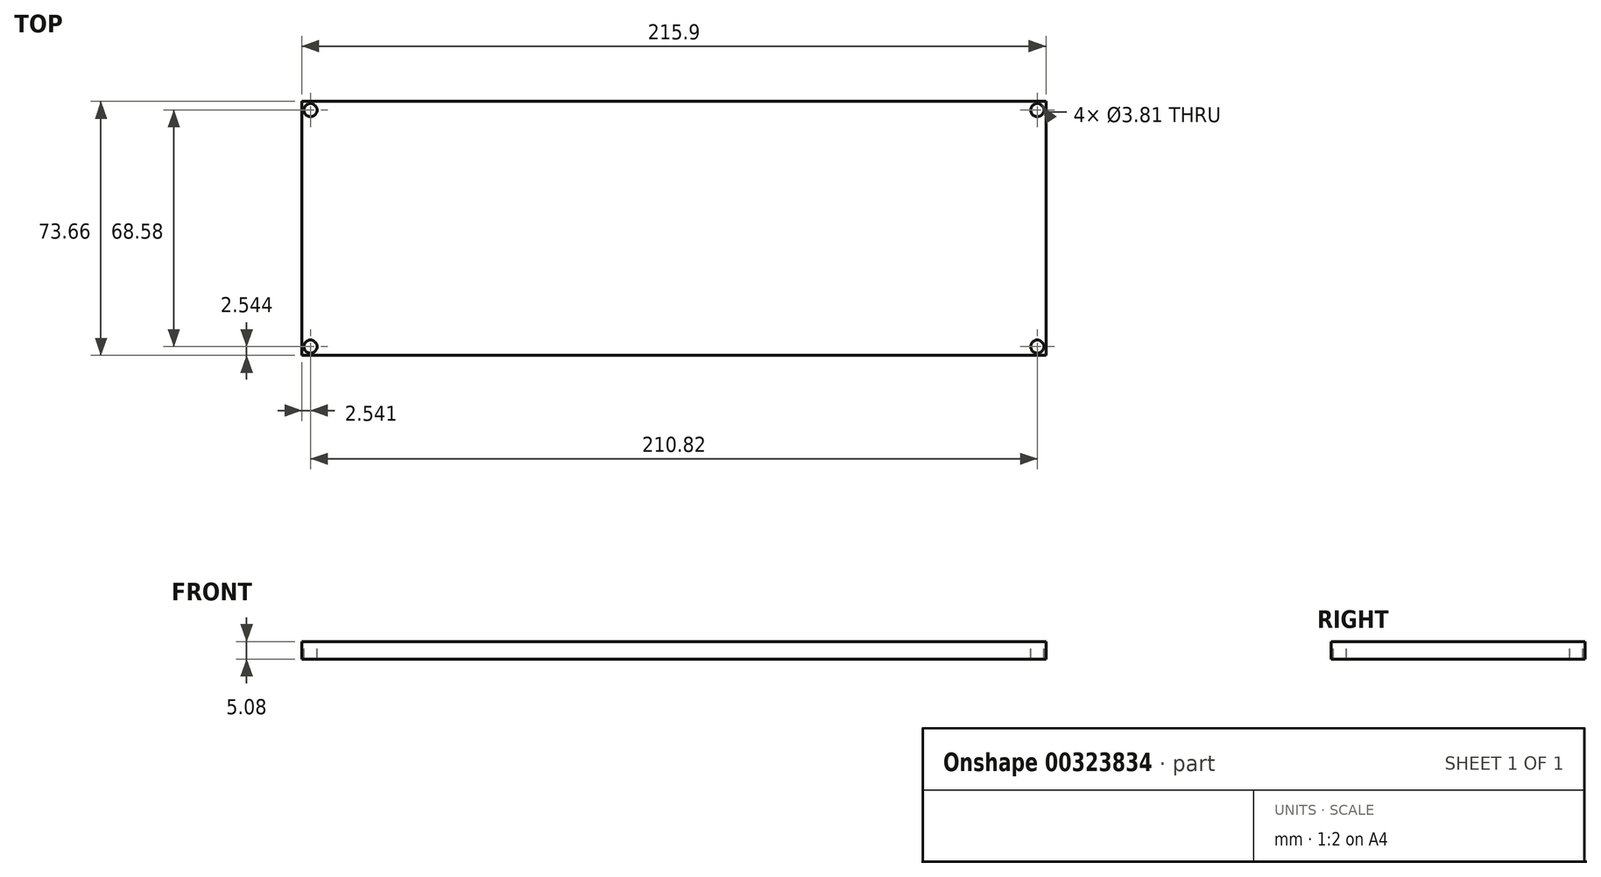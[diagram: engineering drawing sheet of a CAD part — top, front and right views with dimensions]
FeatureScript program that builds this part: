
annotation { "Feature Type Name" : "Feature", "Feature Type Description" : "" }
export const myFeature = defineFeature(function(context is Context, id is Id, definition is map)
    precondition{}
    {
        {
            var Q0;
            Q0=qCreatedBy(makeId("Top.planeOp"),FACE);
            var sketch = newSketch(context, id + "F0", { "sketchPlane" : qUnion([Q0])});
            skLineSegment(sketch, "E0.bottom", {"start": v(-92.09, 42.7) * mm, "end": v(123.81, 42.7) * mm});
            skLineSegment(sketch, "E0.top", {"start": v(-92.09, -30.97) * mm, "end": v(123.81, -30.97) * mm});
            skLineSegment(sketch, "E0.left", {"start": v(-92.09, 42.7) * mm, "end": v(-92.09, -30.97) * mm});
            skLineSegment(sketch, "E0.right", {"start": v(123.81, 42.7) * mm, "end": v(123.81, -30.97) * mm});
            skSolve(sketch);
        }
        {
            var Q0;
            Q0=makeQuery(id+"F0.imprint","IMPRINT",FACE,{"disambiguationData":[TD([[makeQuery(id+"F0.imprint","IMPRINT",EDGE,{"derivedFrom":sQuery(id+"F0.wireOp",EDGE,"E0.bottom")}),-1.0]])]});
            extrude(context, id + "F1", {"entities" : qUnion([Q0]), "depth" : 5.08 * mm});
        }
        {
            var Q0;
            Q0=makeQuery(id+"F1.opExtrude","CAP_FACE",FACE,{"disambiguationData":[OSD([sQuery(id+"F0.wireOp",EDGE,"E0.bottom"),sQuery(id+"F0.wireOp",EDGE,"E0.top"),sQuery(id+"F0.wireOp",EDGE,"E0.left"),sQuery(id+"F0.wireOp",EDGE,"E0.right")])],"isStart":false});
            var sketch = newSketch(context, id + "F2", { "sketchPlane" : qUnion([Q0])});
            skCircle(sketch, "E1", {"center": v(-89.55, 40.15) * mm, "radius": 1.9 * mm});
            skCircle(sketch, "E2", {"center": v(121.27, 40.15) * mm, "radius": 1.9 * mm});
            skCircle(sketch, "E3", {"center": v(121.27, -28.43) * mm, "radius": 1.9 * mm});
            skCircle(sketch, "E4", {"center": v(-89.55, -28.43) * mm, "radius": 1.9 * mm});
            skSolve(sketch);
        }
        {
            var Q0;
            Q0=makeQuery(id+"F2.imprint","IMPRINT",FACE,{"disambiguationData":[TD([[makeQuery(id+"F2.imprint","IMPRINT",EDGE,{"derivedFrom":sQuery(id+"F2.wireOp",EDGE,"E1")}),1.0]])]});
            var Q1;
            Q1=makeQuery(id+"F2.imprint","IMPRINT",FACE,{"disambiguationData":[TD([[makeQuery(id+"F2.imprint","IMPRINT",EDGE,{"derivedFrom":sQuery(id+"F2.wireOp",EDGE,"E2")}),1.0]])]});
            var Q2;
            Q2=makeQuery(id+"F2.imprint","IMPRINT",FACE,{"disambiguationData":[TD([[makeQuery(id+"F2.imprint","IMPRINT",EDGE,{"derivedFrom":sQuery(id+"F2.wireOp",EDGE,"E3")}),1.0]])]});
            var Q3;
            Q3=makeQuery(id+"F2.imprint","IMPRINT",FACE,{"disambiguationData":[TD([[makeQuery(id+"F2.imprint","IMPRINT",EDGE,{"derivedFrom":sQuery(id+"F2.wireOp",EDGE,"E4")}),1.0]])]});
            extrude(context, id + "F3", {"entities" : qUnion([Q0, Q1, Q2, Q3]), "operationType" : NewBodyOperationType.REMOVE, "endBound" : BoundingType.THROUGH_ALL, "oppositeDirection" : true, "depth" : 25.4 * mm});
        }
    });
